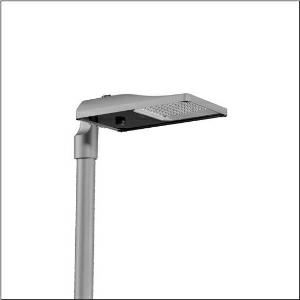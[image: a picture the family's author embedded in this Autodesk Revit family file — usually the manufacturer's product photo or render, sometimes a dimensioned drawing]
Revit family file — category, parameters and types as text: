
# Revit family: streetlight_sl_31_midi___pl52_5xh7h31t08ma_deac
name_source: partatom
category: Lighting Fixtures
units: mm (PartAtom-declared; Revit-internal decimal feet)

## family parameters
Cut with Voids When Loaded = No
Host = Face
Light Source = No
Part Type = Normal
Room Calculation Point = No
Round Connector Dimension = Use Diameter
Shared = No

## types (1)
- --- (1 x LED, 18970 lm, 142.8 W, 3000K)
    Apparent Load = 143 VA
    CIE Flux Codes = 27 59 98 100 100
    Color Rendering = 70
    Color Temperature = 3000K
    Default Elevation = 1800 mm
    Description = Streetlight SL 31 midi D4i, Desk-Remote mast luminaire for post-top, side-entry; light control with lens of PMMA; light distribution: PL52, direct asymmetric distribution, for standard-compliant lighting for roads and squares; LED: luminous flux: 18.970lm, light colour: 730, colour temperature: 3000K; luminous efficacy: 132,8lm/W; control: pre-setting: logarithmic dimming characteristic, flexible luminous flux parameterisation, time-dependent luminous flux control, constant luminous flux control, power reduction, intelligent temperature release in ECG and LED module, overheat protection; luminaire housing, of diecast aluminium, SITECO metallic grey (DB 702S), corrosivity category C5 high according to DIN EN ISO 12944; cover of toughened safety glass, transparent, opened without tools; mast flange of diecast aluminium, SITECO metallic grey (DB 702S), spigot size: 76/60mm, mast flange included unmounted; cable length: 12,5m, connection cable pre-assembled; mains connection: 220..240V, AC, 50/60Hz; power consumption (at start of service life): 142,8W / (at end of service life): 158,8W / (with reduced operation 50%): 60W; protection rating (complete): IP66; insulation class (complete): insulation class II (safety insulation); impact resistance: IK09; certification: CE, ENEC, ENEC+, VDE, UKCA, ZD4i; permissible operating ambient temperature for outdoor applications: -40..+50°C; packaging unit: 1 piece

Light Distribution: PL52
    Height = 79 mm
    Lamp = 1 x LED
    Lamp Light Flux = 18970 lm
    Lamp Power = 142.8 W
    Lamp count = 1
    Length = 577 mm
    Luminous efficacy = 133 lm/W
    Manufacturer = Siteco
    ModVariant = No
    Model = 5XH7H31T08MA
    Number of Poles = 1
    OnlyDefault = Yes
    Power Factor = 1
    Product Name = Streetlight SL 31 midi | PL52
    Product group = mast luminaire | pylon top
    ProductGroupID = 6100
    Protection Class = Protection class II
    Protection Degree = IP 66
    RLX_Detail_Level = 1
    RLX_Emergency_Light_Flux = 0 lm
    RLX_Emergency_Type = 0
    RLX_Emergency_Type_DB = No
    RlxData = <blob elided: 52681 chars, md5=0da292c4>
    Socket = socket
    Standby Power = 0 W
    System Light Flux = 18970 lm
    System Power = 143 W
    Type Comments = factory setting: luminous flux: 100 % | dim-lin: 254 | 735 mA
    Type Image = l_1300321.jpg
    URL = http://relux.com
    VarID = @adj_064197
    Voltage = 0 V
    Weight = 0.00 kg
    Width = 362 mm

## geometry (parser evidence)
native form markers: Blend x4, Sweep x10
no freeform markers — native parametric forms only
